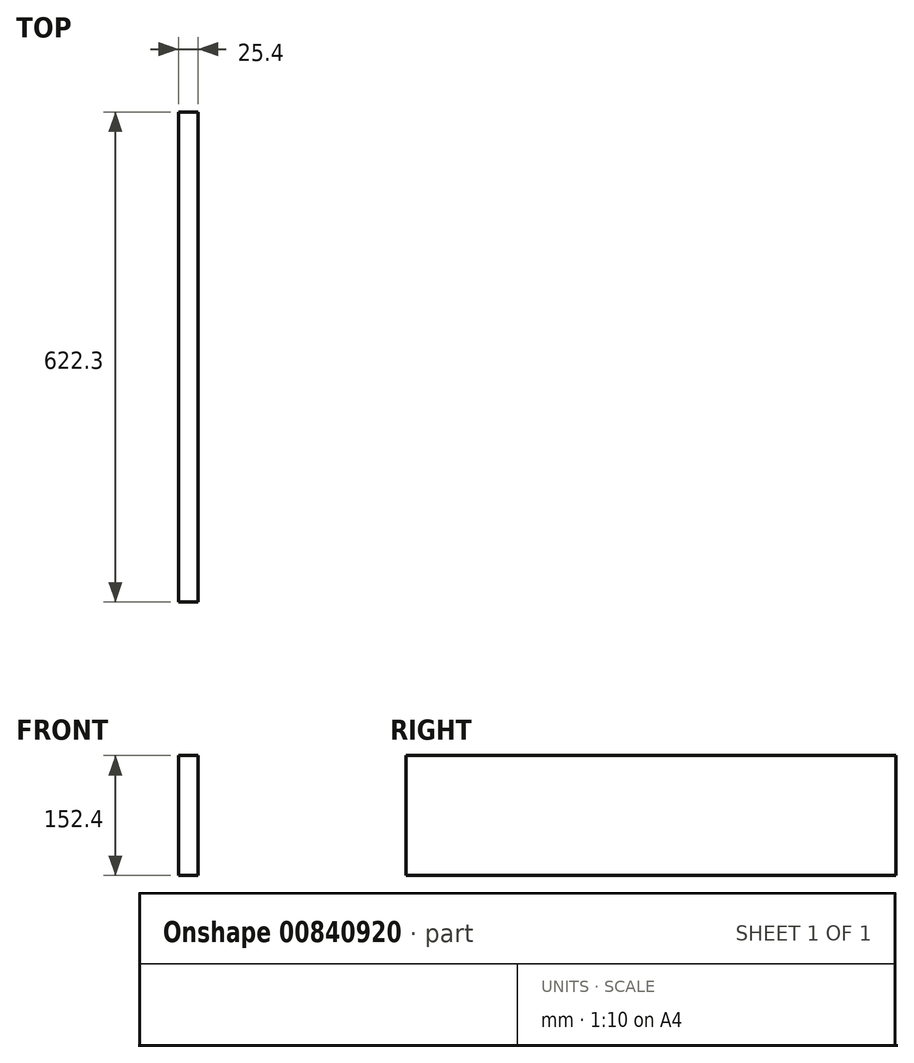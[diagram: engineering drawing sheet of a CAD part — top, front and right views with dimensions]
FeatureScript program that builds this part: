
annotation { "Feature Type Name" : "Feature", "Feature Type Description" : "" }
export const myFeature = defineFeature(function(context is Context, id is Id, definition is map)
    precondition{}
    {
        {
            var Q0;
            Q0=qCreatedBy(makeId("Right.planeOp"),FACE);
            var sketch = newSketch(context, id + "F0", { "sketchPlane" : qUnion([Q0])});
            skLineSegment(sketch, "E0.bottom", {"start": v(0, 0) * mm, "end": v(622.3, 0) * mm});
            skLineSegment(sketch, "E0.top", {"start": v(0, 152.4) * mm, "end": v(622.3, 152.4) * mm});
            skLineSegment(sketch, "E0.left", {"start": v(0, 0) * mm, "end": v(0, 152.4) * mm});
            skLineSegment(sketch, "E0.right", {"start": v(622.3, 0) * mm, "end": v(622.3, 152.4) * mm});
            skSolve(sketch);
        }
        {
            var Q0;
            Q0=makeQuery(id+"F0.imprint","IMPRINT",FACE,{"disambiguationData":[TD([[makeQuery(id+"F0.imprint","IMPRINT",EDGE,{"derivedFrom":sQuery(id+"F0.wireOp",EDGE,"E0.bottom")}),1.0]])]});
            extrude(context, id + "F1", {"entities" : qUnion([Q0]), "depth" : 25.4 * mm, "offsetDistance" : 25.4 * mm});
        }
    });
